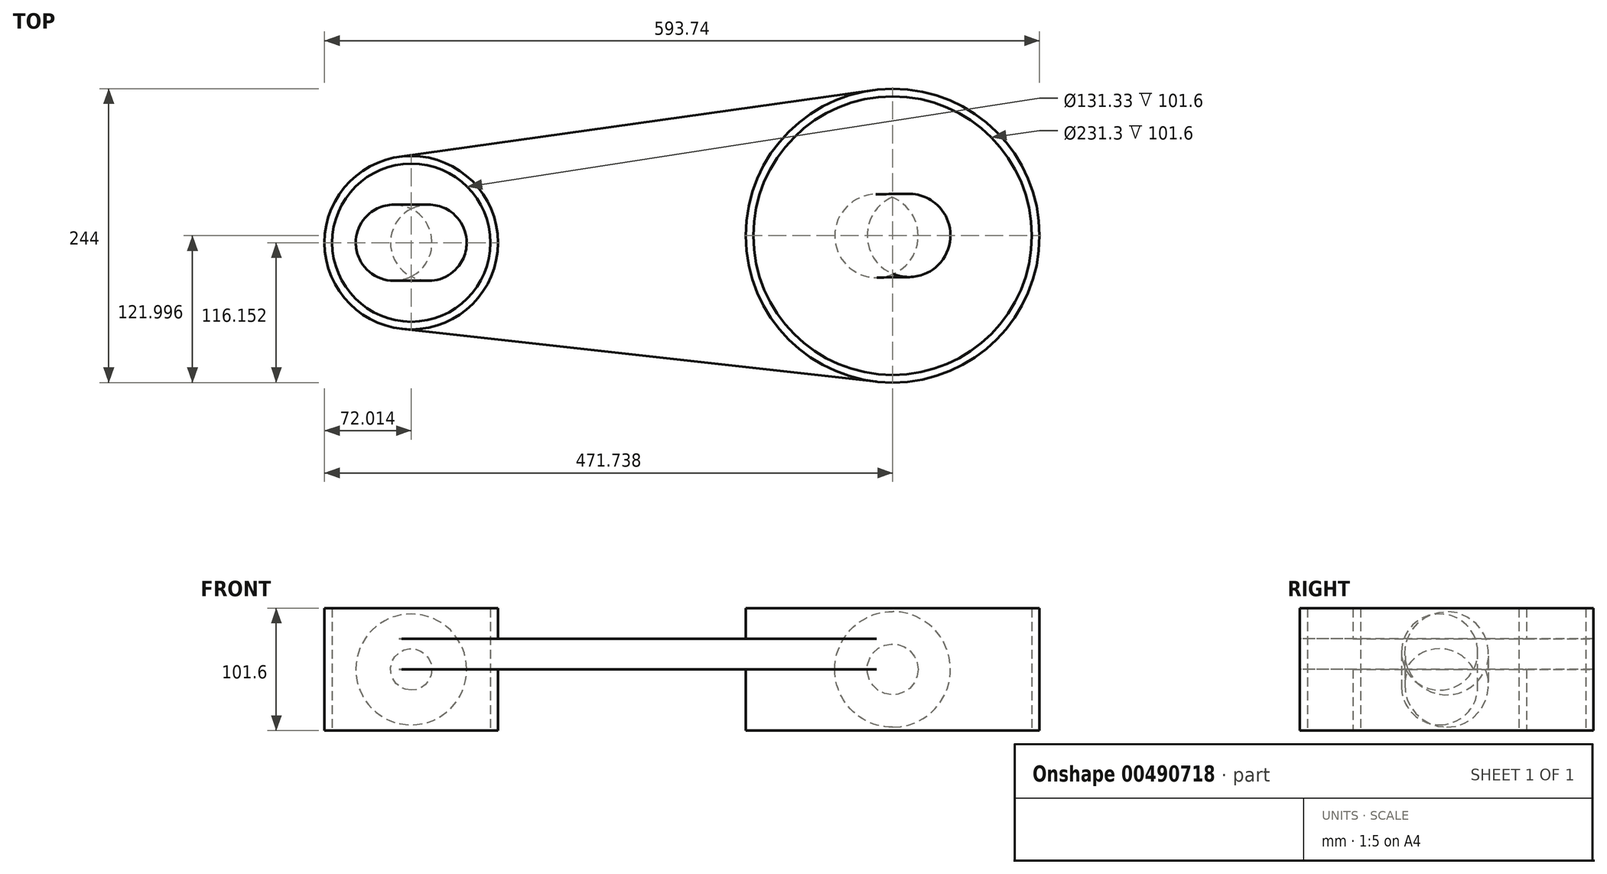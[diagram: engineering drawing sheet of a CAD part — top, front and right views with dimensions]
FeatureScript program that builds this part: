
annotation { "Feature Type Name" : "Feature", "Feature Type Description" : "" }
export const myFeature = defineFeature(function(context is Context, id is Id, definition is map)
    precondition{}
    {
        {
            var Q0;
            Q0=qCreatedBy(makeId("Top.planeOp"),FACE);
            var sketch = newSketch(context, id + "F0", { "sketchPlane" : qUnion([Q0])});
            skCircle(sketch, "E0", {"center": v(-130.42, 174.88) * mm, "radius": 65.67 * mm});
            skCircle(sketch, "E1", {"center": v(269.3, 180.73) * mm, "radius": 115.65 * mm});
            skLineSegment(sketch, "E2", {"start": v(-130.42, 174.88) * mm, "end": v(269.3, 180.73) * mm});
            skCircle(sketch, "E3.0", {"center": v(269.3, 180.73) * mm, "radius": 122 * mm});
            skCircle(sketch, "E4.0", {"center": v(-130.42, 174.88) * mm, "radius": 72.02 * mm});
            skLineSegment(sketch, "E5", {"start": v(-140.46, 246.2) * mm, "end": v(252.29, 301.53) * mm});
            skLineSegment(sketch, "E6.MirrorCS", {"start": v(-138.37, 103.3) * mm, "end": v(255.83, 59.47) * mm});
            skSolve(sketch);
        }
        {
            var Q0;
            {var subQ5=sQuery(id+"F0.wireOp",EDGE,"E5");Q0=makeQuery(id+"F0.imprint","IMPRINT",FACE,{"disambiguationData":[TD([[makeQuery(id+"F0.imprint","IMPRINT",EDGE,{"derivedFrom":subQ5}),-1.0]])]});}
            var Q1;
            {var subQ5=sQuery(id+"F0.wireOp",EDGE,"E6.MirrorCS");Q1=makeQuery(id+"F0.imprint","IMPRINT",FACE,{"disambiguationData":[TD([[makeQuery(id+"F0.imprint","IMPRINT",EDGE,{"derivedFrom":subQ5}),1.0]])]});}
            extrude(context, id + "F1", {"entities" : qUnion([Q0, Q1]), "depth" : 25.4 * mm});
        }
        {
            var Q0;
            Q0=makeQuery(id+"F0.imprint","IMPRINT",FACE,{"disambiguationData":[TD([[makeQuery(id+"F0.imprint","IMPRINT",EDGE,{"derivedFrom":sQuery(id+"F0.wireOp",EDGE,"E0")}),-1.0]])]});
            var Q1;
            Q1=makeQuery(id+"F0.imprint","IMPRINT",FACE,{"disambiguationData":[TD([[makeQuery(id+"F0.imprint","IMPRINT",EDGE,{"derivedFrom":sQuery(id+"F0.wireOp",EDGE,"E1")}),-1.0]])]});
            extrude(context, id + "F2", {"entities" : qUnion([Q0, Q1]), "operationType" : NewBodyOperationType.ADD, "endBound" : BoundingType.SYMMETRIC, "depth" : 101.6 * mm});
        }
        {
            var Q0;
            Q0=makeQuery(id+"F0.imprint","IMPRINT",FACE,{"disambiguationData":[TD([[makeQuery(id+"F0.imprint","IMPRINT",EDGE,{"derivedFrom":sQuery(id+"F0.wireOp",EDGE,"E1")}),1.0]])]});
            var sketch = newSketch(context, id + "F3", { "sketchPlane" : qUnion([Q0])});
            skPoint(sketch, "E7.0", {"position": v(269.3, 180.73) * mm});
            skLineSegment(sketch, "E8.0", {"start": v(-130.42, 174.88) * mm, "end": v(269.3, 180.73) * mm});
            skLineSegment(sketch, "E9", {"start": v(268.84, 212.6) * mm, "end": v(269.77, 148.85) * mm});
            skArc(sketch, "E10", {"start": v(269.77, 148.85) * mm, "mid": v(317.35, 181.43) * mm, "end": v(268.84, 212.6) * mm});
            skSolve(sketch);
        }
        {
            var Q0;
            Q0 = qSketchRegion(id + "F3", true);
            var Q1;
            Q1=sQuery(id+"F3.wireOp",EDGE,"E9");
            revolve(context, id + "F4", {"entities" : qUnion([Q0]), "axis" : qUnion([Q1]), "revolveType" : RevolveType.FULL});
        }
        {
            var Q0;
            Q0=makeQuery(id+"F0.imprint","IMPRINT",FACE,{"disambiguationData":[TD([[makeQuery(id+"F0.imprint","IMPRINT",EDGE,{"derivedFrom":sQuery(id+"F0.wireOp",EDGE,"E0")}),1.0]])]});
            var sketch = newSketch(context, id + "F5", { "sketchPlane" : qUnion([Q0])});
            skLineSegment(sketch, "E11", {"start": v(-130.42, 203.04) * mm, "end": v(-130.42, 146.72) * mm});
            skLineSegment(sketch, "E12.0", {"start": v(-130.42, 174.88) * mm, "end": v(269.3, 180.73) * mm});
            skArc(sketch, "E13", {"start": v(-130.42, 203.04) * mm, "mid": v(-176.46, 174.88) * mm, "end": v(-130.42, 146.72) * mm});
            skSolve(sketch);
        }
        {
            var Q0;
            Q0 = qSketchRegion(id + "F5", true);
            var Q1;
            Q1=sQuery(id+"F5.wireOp",EDGE,"E11");
            revolve(context, id + "F6", {"entities" : qUnion([Q0]), "axis" : qUnion([Q1]), "revolveType" : RevolveType.FULL});
        }
    });
